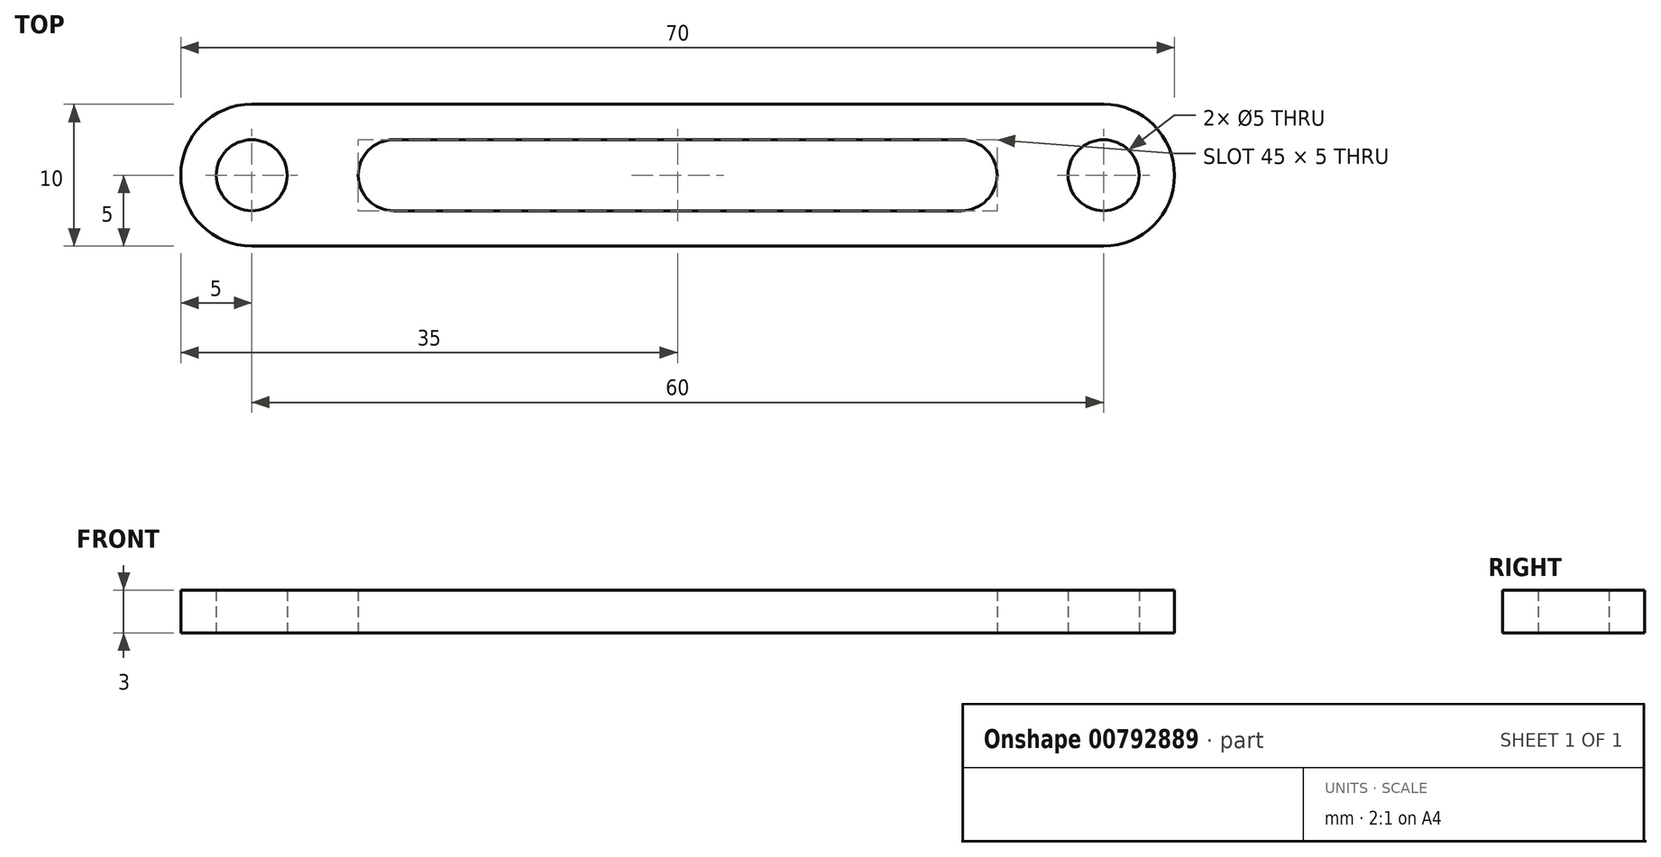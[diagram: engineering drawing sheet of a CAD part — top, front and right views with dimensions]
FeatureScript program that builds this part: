
annotation { "Feature Type Name" : "Feature", "Feature Type Description" : "" }
export const myFeature = defineFeature(function(context is Context, id is Id, definition is map)
    precondition{}
    {
        {
            var Q0;
            Q0=qCreatedBy(makeId("Top.planeOp"),FACE);
            var sketch = newSketch(context, id + "F0", { "sketchPlane" : qUnion([Q0])});
            skArc(sketch, "E0", {"start": v(0, 5) * mm, "mid": v(-5, 0) * mm, "end": v(0, -5) * mm});
            skArc(sketch, "E1", {"start": v(60, -5) * mm, "mid": v(65, 0) * mm, "end": v(60, 5) * mm});
            skLineSegment(sketch, "E2", {"start": v(0, -5) * mm, "end": v(60, -5) * mm});
            skLineSegment(sketch, "E3", {"start": v(60, 5) * mm, "end": v(0, 5) * mm});
            skCircle(sketch, "E4", {"center": v(0, 0) * mm, "radius": 2.5 * mm});
            skCircle(sketch, "E5", {"center": v(60, 0) * mm, "radius": 2.5 * mm});
            skArc(sketch, "E6", {"start": v(10, 2.5) * mm, "mid": v(7.5, 0) * mm, "end": v(10, -2.5) * mm});
            skArc(sketch, "E7", {"start": v(50, -2.5) * mm, "mid": v(52.5, 0) * mm, "end": v(50, 2.5) * mm});
            skLineSegment(sketch, "E8", {"start": v(10, 2.5) * mm, "end": v(50, 2.5) * mm});
            skLineSegment(sketch, "E9", {"start": v(50, -2.5) * mm, "end": v(10, -2.5) * mm});
            skSolve(sketch);
        }
        {
            var Q0;
            Q0=makeQuery(id+"F0.imprint","IMPRINT",FACE,{"disambiguationData":[TD([[makeQuery(id+"F0.imprint","IMPRINT",EDGE,{"derivedFrom":sQuery(id+"F0.wireOp",EDGE,"E0")}),1.0]])]});
            extrude(context, id + "F1", {"entities" : qUnion([Q0]), "depth" : 3 * mm, "offsetDistance" : 25 * mm});
        }
    });
